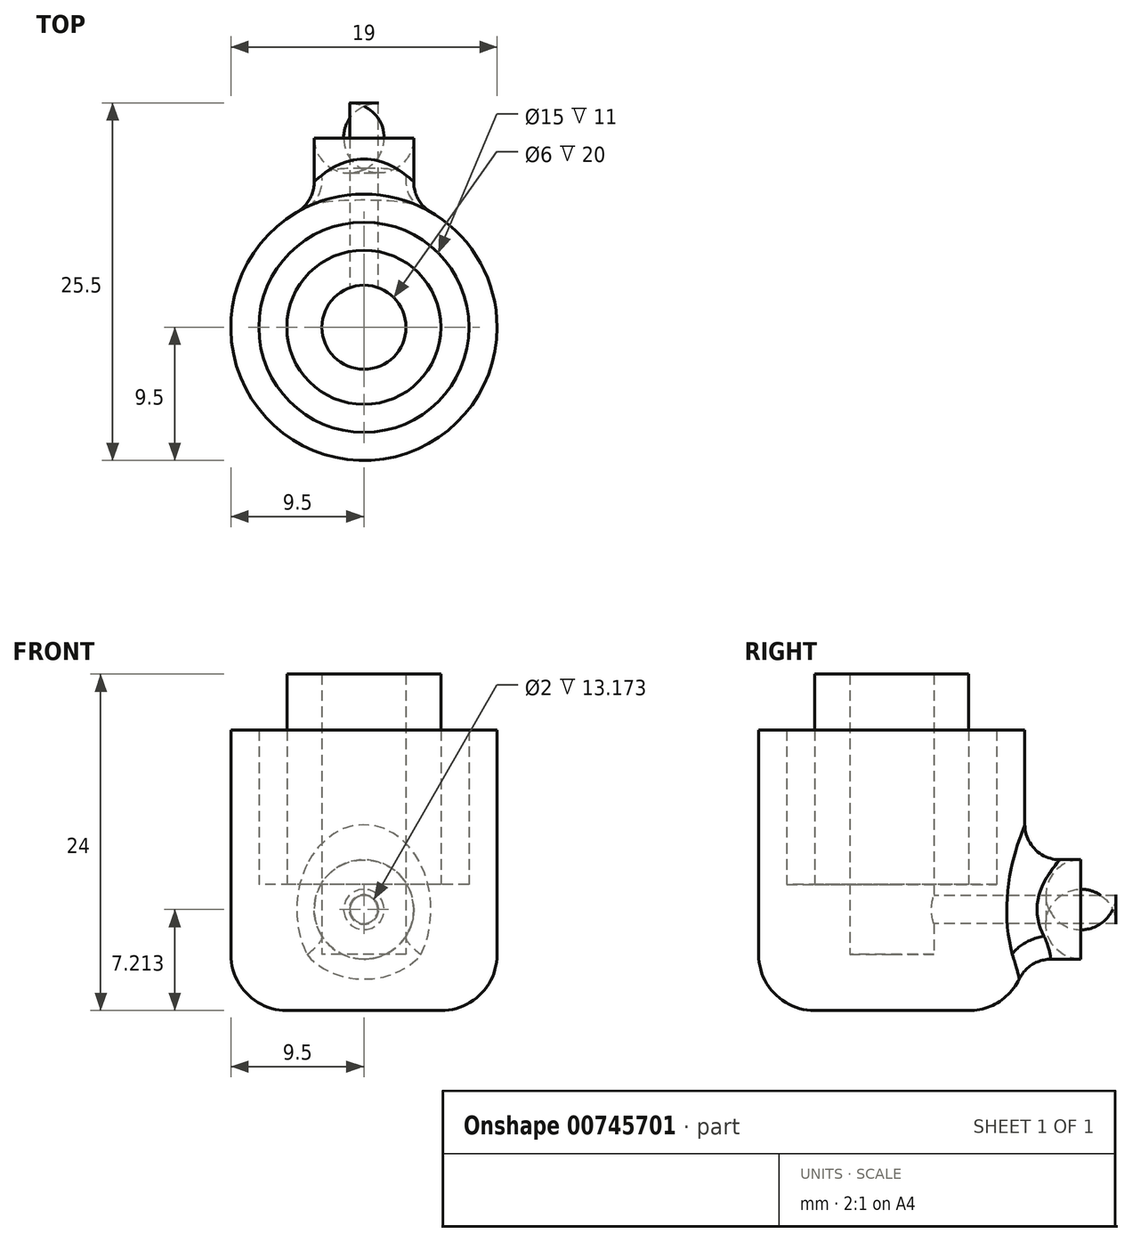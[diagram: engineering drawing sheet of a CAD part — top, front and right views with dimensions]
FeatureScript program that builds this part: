
annotation { "Feature Type Name" : "Feature", "Feature Type Description" : "" }
export const myFeature = defineFeature(function(context is Context, id is Id, definition is map)
    precondition{}
    {
        {
            var Q0;
            Q0=qCreatedBy(makeId("Top.planeOp"),FACE);
            var sketch = newSketch(context, id + "F0", { "sketchPlane" : qUnion([Q0])});
            skCircle(sketch, "E0", {"center": v(0, 0) * mm, "radius": 7.5 * mm});
            skCircle(sketch, "E1", {"center": v(0, 0) * mm, "radius": 9.5 * mm});
            skSolve(sketch);
        }
        {
            var Q0;
            Q0=makeQuery(id+"F0.imprint","IMPRINT",FACE,{"disambiguationData":[TD([[makeQuery(id+"F0.imprint","IMPRINT",EDGE,{"derivedFrom":sQuery(id+"F0.wireOp",EDGE,"E0")}),-1.0]])]});
            extrude(context, id + "F1", {"entities" : qUnion([Q0]), "depth" : 20 * mm, "offsetDistance" : 25 * mm});
        }
        {
            var Q0;
            Q0=makeQuery(id+"F0.imprint","IMPRINT",FACE,{"disambiguationData":[TD([[makeQuery(id+"F0.imprint","IMPRINT",EDGE,{"derivedFrom":sQuery(id+"F0.wireOp",EDGE,"E0")}),1.0]])]});
            extrude(context, id + "F2", {"entities" : qUnion([Q0]), "operationType" : NewBodyOperationType.ADD, "depth" : 4 * mm, "offsetDistance" : 25 * mm});
        }
        {
            var Q0;
            Q0=makeQuery(id+"F1.opExtrude","CAP_EDGE",EDGE,{"disambiguationData":[OSD([sQuery(id+"F0.wireOp",EDGE,"E1")])],"isStart":true});
            fillet(context, id + "F3", {"entities" : qUnion([Q0]), "radius" : 4 * mm, "tangentPropagation" : true, "allowEdgeOverflow" : false});
        }
        {
            var Q0;
            Q0=makeQuery(id+"F2.opExtrude","CAP_FACE",FACE,{"disambiguationData":[OSD([sQuery(id+"F0.wireOp",EDGE,"E0")])],"isStart":false});
            var sketch = newSketch(context, id + "F4", { "sketchPlane" : qUnion([Q0])});
            skCircle(sketch, "E2", {"center": v(0, 0) * mm, "radius": 5.5 * mm});
            skCircle(sketch, "E3", {"center": v(0, 0) * mm, "radius": 3 * mm});
            skSolve(sketch);
        }
        {
            var Q0;
            Q0=makeQuery(id+"F4.imprint","IMPRINT",FACE,{"disambiguationData":[TD([[makeQuery(id+"F4.imprint","IMPRINT",EDGE,{"derivedFrom":sQuery(id+"F4.wireOp",EDGE,"E2")}),1.0]])]});
            extrude(context, id + "F5", {"entities" : qUnion([Q0]), "operationType" : NewBodyOperationType.ADD, "depth" : 20 * mm, "offsetDistance" : 25 * mm});
        }
        {
            var Q0;
            {var subQ0=sQuery(id+"F0.wireOp",EDGE,"E0");Q0=makeQuery(id+"F5.boolean.opBoolean","SPLIT",FACE,{"disambiguationData":[TD([makeQuery(id+"F1.opExtrude","SWEPT_FACE",FACE,{"disambiguationData":[OSD([subQ0])]})])],"derivedFrom":makeQuery(id+"F2.opExtrude","CAP_FACE",FACE,{"disambiguationData":[OSD([subQ0])],"isStart":false})});}
            extrude(context, id + "F6", {"entities" : qUnion([Q0]), "operationType" : NewBodyOperationType.ADD, "depth" : 5 * mm, "offsetDistance" : 25 * mm});
        }
        {
            var Q0;
            Q0=qCreatedBy(makeId("Front.planeOp"),FACE);
            var sketch = newSketch(context, id + "F7", { "sketchPlane" : qUnion([Q0])});
            skCircle(sketch, "E4", {"center": v(0, 7.21) * mm, "radius": 1 * mm});
            skCircle(sketch, "E5", {"center": v(0, 7.21) * mm, "radius": 3.55 * mm});
            skSolve(sketch);
        }
        {
            var Q0;
            Q0=makeQuery(id+"F7.imprint","IMPRINT",FACE,{"disambiguationData":[TD([[makeQuery(id+"F7.imprint","IMPRINT",EDGE,{"derivedFrom":sQuery(id+"F7.wireOp",EDGE,"E4")}),1.0]])]});
            extrude(context, id + "F8", {"entities" : qUnion([Q0]), "operationType" : NewBodyOperationType.REMOVE, "oppositeDirection" : true, "depth" : 25 * mm, "offsetDistance" : 25 * mm});
        }
        {
            var Q0;
            Q0=makeQuery(id+"F7.imprint","IMPRINT",FACE,{"disambiguationData":[TD([[makeQuery(id+"F7.imprint","IMPRINT",EDGE,{"derivedFrom":sQuery(id+"F7.wireOp",EDGE,"E4")}),-1.0]])]});
            extrude(context, id + "F9", {"entities" : qUnion([Q0]), "operationType" : NewBodyOperationType.ADD, "oppositeDirection" : true, "depth" : 16 * mm, "offsetDistance" : 25 * mm, "hasSecondDirection" : true, "secondDirectionOppositeDirection" : true, "secondDirectionDepth" : 8.4 * mm});
        }
        {
            var Q0;
            Q0=makeQuery(id+"F9.opExtrude","CAP_EDGE",EDGE,{"disambiguationData":[OSD([sQuery(id+"F7.wireOp",EDGE,"E5")])],"isStart":false});
            var Q1;
            Q1=makeQuery(id+"F9.boolean.opBoolean","INTERSECT",EDGE,{"derivedFrom":[makeQuery(id+"F1.opExtrude","SWEPT_FACE",FACE,{"disambiguationData":[OSD([sQuery(id+"F0.wireOp",EDGE,"E1")])]}),makeQuery(id+"F9.opExtrude","SWEPT_FACE",FACE,{"disambiguationData":[OSD([sQuery(id+"F7.wireOp",EDGE,"E5")])]})]});
            fillet(context, id + "F10", {"entities" : qUnion([Q0, Q1]), "radius" : 2.5 * mm, "tangentPropagation" : true, "allowEdgeOverflow" : false});
        }
    });
